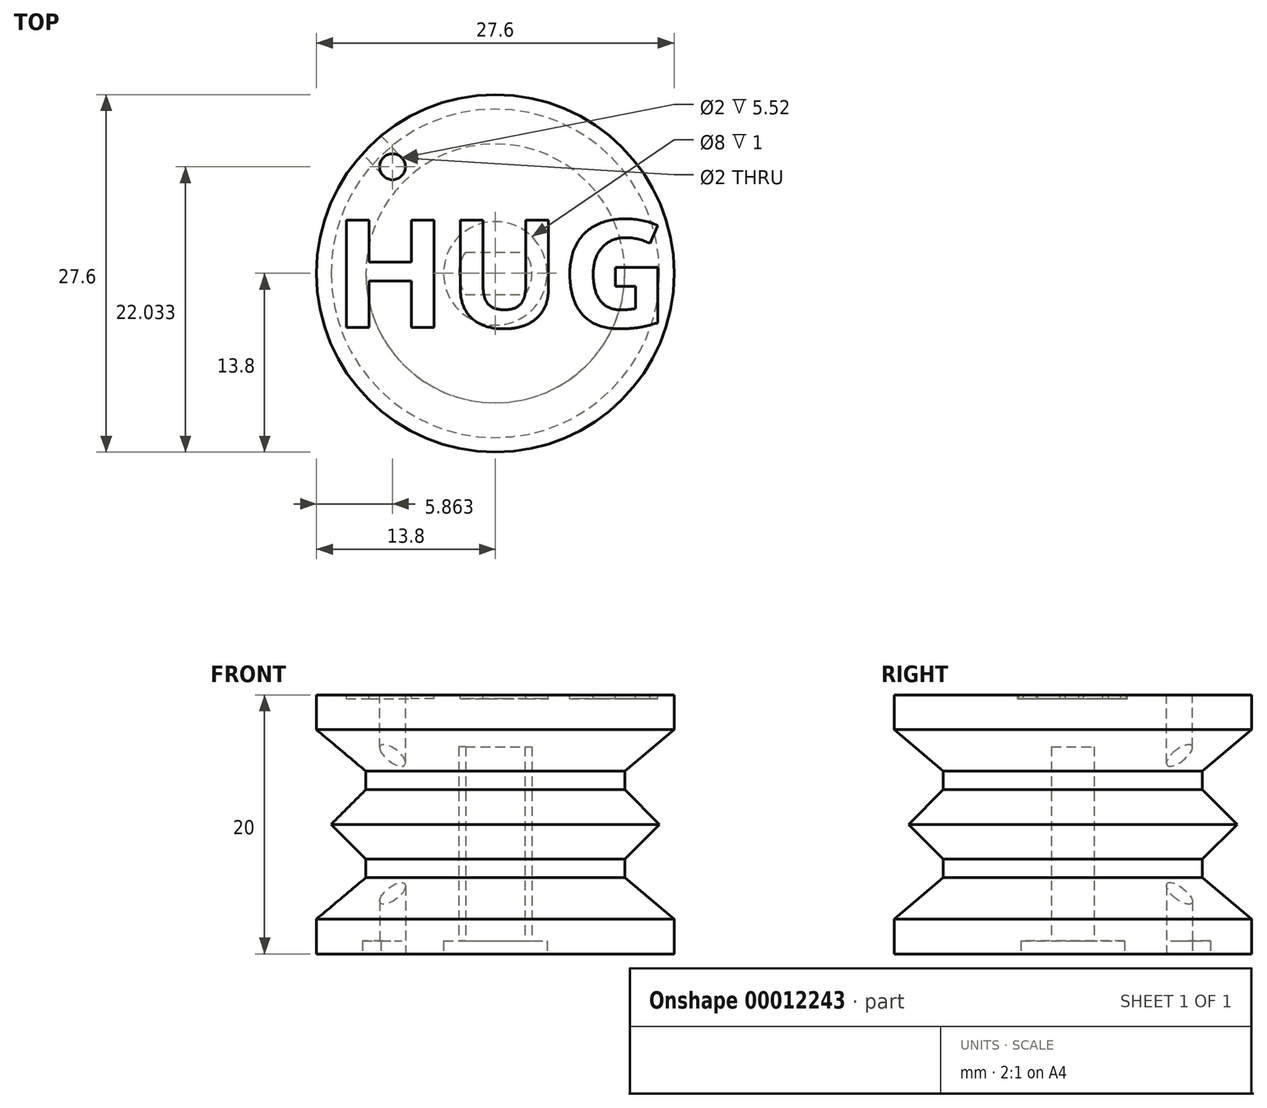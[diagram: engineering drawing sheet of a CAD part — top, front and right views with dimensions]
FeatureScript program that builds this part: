
annotation { "Feature Type Name" : "Feature", "Feature Type Description" : "" }
export const myFeature = defineFeature(function(context is Context, id is Id, definition is map)
    precondition{}
    {
        {
            var Q0;
            Q0=qCreatedBy(makeId("Top.planeOp"),FACE);
            var sketch = newSketch(context, id + "F0", { "sketchPlane" : qUnion([Q0])});
            skCircle(sketch, "E0", {"center": v(0, 0) * mm, "radius": 10 * mm});
            skLineSegment(sketch, "E1", {"start": v(0, -10) * mm, "end": v(0, 10) * mm});
            skSolve(sketch);
        }
        {
            var Q0;
            Q0 = qSketchRegion(id + "F0", true);
            extrude(context, id + "F1", {"entities" : qUnion([Q0]), "endBound" : BoundingType.SYMMETRIC, "depth" : 20 * mm});
        }
        {
            var Q0;
            Q0=qCreatedBy(makeId("Right.planeOp"),FACE);
            var sketch = newSketch(context, id + "F2", { "sketchPlane" : qUnion([Q0])});
            skLineSegment(sketch, "E2", {"start": v(-9.54, -10) * mm, "end": v(-13.8, -10) * mm});
            skLineSegment(sketch, "E3", {"start": v(-13.8, -10) * mm, "end": v(-13.8, -7.3) * mm});
            skLineSegment(sketch, "E4", {"start": v(-13.8, -7.3) * mm, "end": v(-9.54, -3.73) * mm});
            skLineSegment(sketch, "E5", {"start": v(-9.54, -3.73) * mm, "end": v(-9.54, -10) * mm});
            skSolve(sketch);
        }
        {
            var Q0;
            Q0=makeQuery(id+"F2.imprint","IMPRINT",FACE,{"disambiguationData":[TD([[makeQuery(id+"F2.imprint","IMPRINT",EDGE,{"derivedFrom":sQuery(id+"F2.wireOp",EDGE,"E2")}),-1.0]])]});
            var Q1;
            Q1=makeQuery(id+"F1.opExtrude","CAP_EDGE",EDGE,{"disambiguationData":[OSD([sQuery(id+"F0.wireOp",EDGE,"E0")])],"isStart":false});
            revolve(context, id + "F3", {"operationType" : NewBodyOperationType.ADD, "entities" : qUnion([Q0]), "axis" : qUnion([Q1]), "revolveType" : RevolveType.FULL});
        }
        {
            var Q0;
            Q0=makeQuery(id+"F1.opExtrude","CAP_FACE",FACE,{"disambiguationData":[OSD([sQuery(id+"F0.wireOp",EDGE,"E0")])],"isStart":true});
            var sketch = newSketch(context, id + "F4", { "sketchPlane" : qUnion([Q0])});
            skCircle(sketch, "E6", {"center": v(-7.94, -8.23) * mm, "radius": 1 * mm});
            skSolve(sketch);
        }
        {
            var Q0;
            Q0 = qSketchRegion(id + "F4", true);
            extrude(context, id + "F5", {"entities" : qUnion([Q0]), "operationType" : NewBodyOperationType.REMOVE, "oppositeDirection" : true, "depth" : 7 * mm});
        }
        {
            var Q0;
            Q0=makeQuery(id+"F3.opRevolve","SWEPT_BODY",BODY,{"disambiguationData":[OSD([sQuery(id+"F2.wireOp",EDGE,"E2"),sQuery(id+"F2.wireOp",EDGE,"E3"),sQuery(id+"F2.wireOp",EDGE,"E4"),sQuery(id+"F2.wireOp",EDGE,"E5")])]});
            var Q1;
            Q1=makeQuery(id+"F1.opExtrude","SWEPT_BODY",BODY,{"disambiguationData":[OSD([sQuery(id+"F0.wireOp",EDGE,"E0")])]});
            var Q2;
            Q2=qCreatedBy(makeId("Top.planeOp"),FACE);
            mirror(context, id + "F6", {"operationType" : NewBodyOperationType.ADD, "entities" : qUnion([Q0, Q1]), "mirrorPlane" : qUnion([Q2])});
        }
        {
            var Q0;
            Q0=makeQuery(id+"F3.boolean.opBoolean","MERGE",FACE,{"derivedFrom":[makeQuery(id+"F1.opExtrude","CAP_FACE",FACE,{"disambiguationData":[OSD([sQuery(id+"F0.wireOp",EDGE,"E0")])],"isStart":true}),makeQuery(id+"F3.opRevolve","SWEPT_FACE",FACE,{"disambiguationData":[OSD([sQuery(id+"F2.wireOp",EDGE,"E2")])]})]});
            var sketch = newSketch(context, id + "F7", { "sketchPlane" : qUnion([Q0])});
            skCircle(sketch, "E7", {"center": v(0, 0) * mm, "radius": 4 * mm});
            skSolve(sketch);
        }
        {
            var Q0;
            Q0 = qSketchRegion(id + "F7", true);
            var Q1;
            Q1=makeQuery(id+"F3.boolean.opBoolean","MERGE",FACE,{"derivedFrom":[makeQuery(id+"F1.opExtrude","CAP_FACE",FACE,{"disambiguationData":[OSD([sQuery(id+"F0.wireOp",EDGE,"E0")])],"isStart":true}),makeQuery(id+"F3.opRevolve","SWEPT_FACE",FACE,{"disambiguationData":[OSD([sQuery(id+"F2.wireOp",EDGE,"E2")])]})]});
            extrude(context, id + "F8", {"entities" : qUnion([Q0]), "operationType" : NewBodyOperationType.REMOVE, "oppositeDirection" : true, "endBoundEntity" : qUnion([Q1]), "depth" : 1 * mm});
        }
        {
            var Q0;
            Q0=makeQuery(id+"F8.boolean.opBoolean","COPY",FACE,{"derivedFrom":makeQuery(id+"F8.opExtrude","CAP_FACE",FACE,{"disambiguationData":[OSD([sQuery(id+"F7.wireOp",EDGE,"E7")])],"isStart":false})});
            var sketch = newSketch(context, id + "F9", { "sketchPlane" : qUnion([Q0])});
            skArc(sketch, "E8", {"start": v(-2.3, 1.65) * mm, "mid": v(-2.82, 0) * mm, "end": v(-2.3, -1.65) * mm});
            skLineSegment(sketch, "E9.rect.bottom", {"start": v(-2.3, 1.65) * mm, "end": v(2.3, 1.65) * mm});
            skLineSegment(sketch, "E9.rect.top", {"start": v(-2.3, -1.65) * mm, "end": v(2.3, -1.65) * mm});
            skArc(sketch, "E10.trimOffspring", {"start": v(2.3, -1.65) * mm, "mid": v(2.82, 0) * mm, "end": v(2.3, 1.65) * mm});
            skSolve(sketch);
        }
        {
            var Q0;
            Q0 = qSketchRegion(id + "F9", true);
            extrude(context, id + "F10", {"entities" : qUnion([Q0]), "operationType" : NewBodyOperationType.REMOVE, "oppositeDirection" : true, "depth" : 15 * mm});
        }
        {
            var Q0;
            {var subQ0=sQuery(id+"F0.wireOp",EDGE,"E0");Q0=makeQuery(id+"F6.boolean.opBoolean","MERGE",FACE,{"derivedFrom":[makeQuery(id+"F1.opExtrude","CAP_FACE",FACE,{"disambiguationData":[OSD([subQ0])],"isStart":false}),makeQuery(id+"F6.opPattern","COPY",FACE,{"derivedFrom":makeQuery(id+"F3.boolean.opBoolean","MERGE",FACE,{"derivedFrom":[makeQuery(id+"F1.opExtrude","CAP_FACE",FACE,{"disambiguationData":[OSD([subQ0])],"isStart":true}),makeQuery(id+"F3.opRevolve","SWEPT_FACE",FACE,{"disambiguationData":[OSD([sQuery(id+"F2.wireOp",EDGE,"E2")])]})]}),"instanceName":"1"})]});}
            var sketch = newSketch(context, id + "F11", { "sketchPlane" : qUnion([Q0])});
            skText(sketch, "E11", { "text": "HUG", "fontName": "OpenSans-Bold.ttf"});
            const initialGuessF11  = {"E11": [-0.01254, -0.00417, 1, 0, 0.00834]};
            skSetInitialGuess(sketch, initialGuessF11);
            skSolve(sketch);
        }
        {
            var Q0;
            Q0=makeQuery(id+"F11.imprint","IMPRINT",FACE,{"disambiguationData":[TD([[makeQuery(id+"F11.imprint","IMPRINT",EDGE,{"derivedFrom":sQuery(id+"F11.wireOp",EDGE,"E11.sketch_text.stroke-0")}),-1.0]])]});
            var Q1;
            Q1=makeQuery(id+"F11.imprint","IMPRINT",FACE,{"disambiguationData":[TD([[makeQuery(id+"F11.imprint","IMPRINT",EDGE,{"derivedFrom":sQuery(id+"F11.wireOp",EDGE,"E11.sketch_text.stroke-12")}),-1.0]])]});
            var Q2;
            Q2=makeQuery(id+"F11.imprint","IMPRINT",FACE,{"disambiguationData":[TD([[makeQuery(id+"F11.imprint","IMPRINT",EDGE,{"derivedFrom":sQuery(id+"F11.wireOp",EDGE,"E11.sketch_text.stroke-27")}),-1.0]])]});
            extrude(context, id + "F12", {"entities" : qUnion([Q0, Q1, Q2]), "operationType" : NewBodyOperationType.REMOVE, "oppositeDirection" : true, "depth" : .3 * mm});
        }
        {
            var Q0;
            Q0=qCreatedBy(makeId("Front.planeOp"),FACE);
            var sketch = newSketch(context, id + "F13", { "sketchPlane" : qUnion([Q0])});
            skCircle(sketch, "E12", {"center": v(-9.1, 0) * mm, "radius": 2.53 * mm});
            skCircle(sketch, "E13.cCircle", {"center": v(-9.1, 0) * mm, "radius": 2.53 * mm, "construction": true});
            skLineSegment(sketch, "E13.0", {"start": v(-5.53, 0) * mm, "end": v(-9.1, -3.58) * mm});
            skLineSegment(sketch, "E13.1", {"start": v(-9.1, -3.58) * mm, "end": v(-12.68, 0) * mm});
            skLineSegment(sketch, "E13.2", {"start": v(-12.68, 0) * mm, "end": v(-9.1, 3.58) * mm});
            skLineSegment(sketch, "E13.3", {"start": v(-9.1, 3.58) * mm, "end": v(-5.53, 0) * mm});
            skPoint(sketch, "E13.0.midPoint", {"position": v(-7.31, -1.79) * mm});
            skSolve(sketch);
        }
        {
            var Q0;
            Q0 = qSketchRegion(id + "F13", true);
            var Q1;
            Q1=makeQuery(id+"F1.opExtrude","SWEPT_FACE",FACE,{"disambiguationData":[OSD([sQuery(id+"F0.wireOp",EDGE,"E0")])]});
            revolve(context, id + "F14", {"operationType" : NewBodyOperationType.ADD, "entities" : qUnion([Q0]), "axis" : qUnion([Q1]), "revolveType" : RevolveType.FULL});
        }
        {
            var Q0;
            Q0=makeQuery(id+"F3.boolean.opBoolean","MERGE",FACE,{"derivedFrom":[makeQuery(id+"F1.opExtrude","CAP_FACE",FACE,{"disambiguationData":[OSD([sQuery(id+"F0.wireOp",EDGE,"E0")])],"isStart":true}),makeQuery(id+"F3.opRevolve","SWEPT_FACE",FACE,{"disambiguationData":[OSD([sQuery(id+"F2.wireOp",EDGE,"E2")])]})]});
            var sketch = newSketch(context, id + "F15", { "sketchPlane" : qUnion([Q0])});
            skLineSegment(sketch, "E14", {"start": v(-8.66, -7.55) * mm, "end": v(-10.26, -9.24) * mm});
            skLineSegment(sketch, "E15", {"start": v(-8.82, -10.62) * mm, "end": v(-7.2, -8.92) * mm});
            skSolve(sketch);
        }
        {
            var Q0;
            {var subQ2=sQuery(id+"F15.wireOp",EDGE,"E14");Q0=makeQuery(id+"F15.imprint","IMPRINT",FACE,{"disambiguationData":[TD([[makeQuery(id+"F15.imprint","IMPRINT",EDGE,{"derivedFrom":subQ2}),1.0]])]});}
            extrude(context, id + "F16", {"entities" : qUnion([Q0]), "operationType" : NewBodyOperationType.REMOVE, "oppositeDirection" : true, "depth" : 1 * mm});
        }
    });
